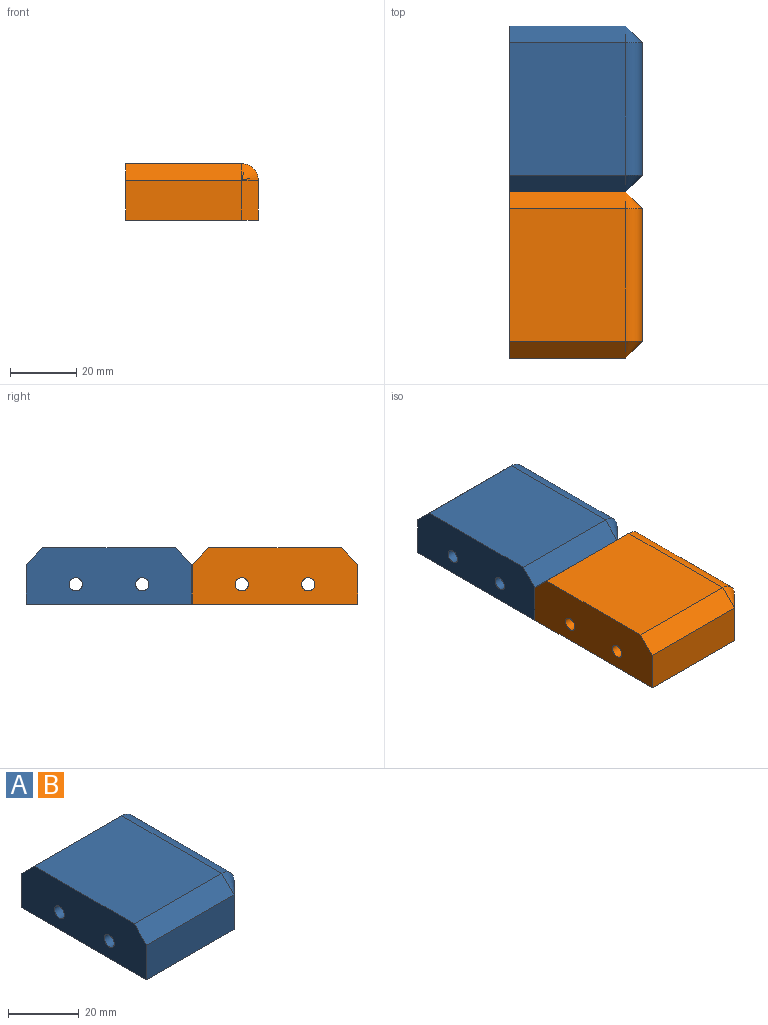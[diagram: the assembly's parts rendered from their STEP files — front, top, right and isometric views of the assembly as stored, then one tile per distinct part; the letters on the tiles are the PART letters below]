
ASSEMBLY  parts=2 mates=1
PART A: 15 faces, bbox 40x50x17 mm
  f0: plane 40x12.01mm, normal (1,0,0), area 455.4mm2, adj f3,f5,f8,f9,f13,f14
  f1: plane 40x35mm, normal (0,0,1), area 1400mm2, adj f2,f5,f6,f11
  f2: plane 50x17.01mm, normal (-1,0,0), area 800.6mm2, adj f1,f3,f4,f6,f9,f10,f11,f14
  f3: plane 50x40mm, normal (0,0,-1), area 1975mm2, adj f0,f2,f4,f8,f10,f13
  f4: plane 35x12.01mm, normal (0,1,0), area 420.5mm2, adj f2,f3,f6,f8
  f5: cylinder r=5mm len=40mm, axis (0,1,0), area 314.2mm2, adj f0,f1,f7,f12
  f6: plane 35x5mm, normal (0,0.71,0.71), area 247.5mm2, adj f1,f2,f4,f7
  f7: cone r=5mm half-angle=45deg, axis (0,-1,0), area 27.8mm2, adj f5,f6,f8
  f8: plane 12.01x5mm, normal (0.71,0.71,0), area 85mm2, adj f0,f3,f4,f7
  f9: cylinder r=2mm len=40mm, axis (1,0,0), area 502.7mm2, adj f0,f2
  f10: plane 35x12.01mm, normal (0,-1,0), area 420.5mm2, adj f2,f3,f11,f13
  f11: plane 35x5mm, normal (0,-0.71,0.71), area 247.5mm2, adj f1,f2,f10,f12
  f12: cone r=5mm half-angle=45deg, axis (0,1,0), area 27.8mm2, adj f5,f11,f13
  f13: plane 12.01x5mm, normal (0.71,-0.71,0), area 85mm2, adj f0,f3,f10,f12
  f14: cylinder r=2mm len=40mm, axis (1,0,0), area 502.7mm2, adj f0,f2
PART B: same geometry as A
PLACE A t=(-81.06,34.67,15.78)mm
PLACE B t=(-81.06,-15.33,15.78)mm
MATE fastened A.f10 <-> B.f4  axis (0,-1,0) through (-103.56,-15.33,21.79)mm
